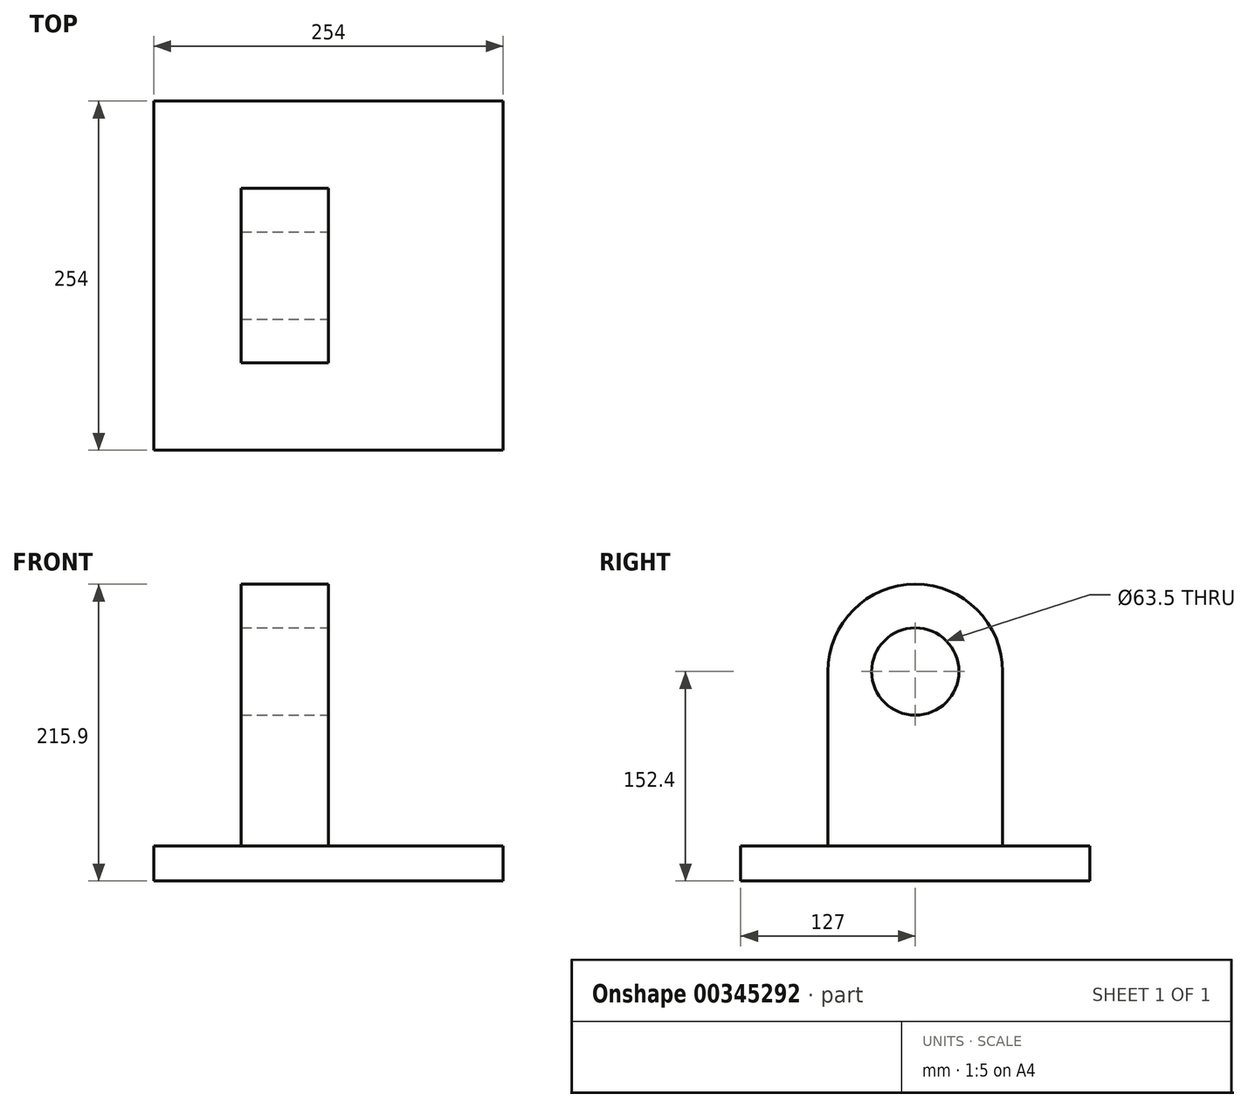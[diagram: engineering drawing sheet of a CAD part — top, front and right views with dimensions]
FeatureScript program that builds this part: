
annotation { "Feature Type Name" : "Feature", "Feature Type Description" : "" }
export const myFeature = defineFeature(function(context is Context, id is Id, definition is map)
    precondition{}
    {
        {
            var Q0;
            Q0=qCreatedBy(makeId("Top.planeOp"),FACE);
            var sketch = newSketch(context, id + "F0", { "sketchPlane" : qUnion([Q0])});
            skLineSegment(sketch, "E0.bottom", {"start": v(127, -127) * mm, "end": v(-127, -127) * mm});
            skLineSegment(sketch, "E0.top", {"start": v(127, 127) * mm, "end": v(-127, 127) * mm});
            skLineSegment(sketch, "E0.left", {"start": v(127, -127) * mm, "end": v(127, 127) * mm});
            skLineSegment(sketch, "E0.right", {"start": v(-127, -127) * mm, "end": v(-127, 127) * mm});
            skPoint(sketch, "E0.middle", {"position": v(0, 0) * mm});
            skSolve(sketch);
        }
        {
            var Q0;
            Q0=makeQuery(id+"F0.imprint","IMPRINT",FACE,{"disambiguationData":[TD([[makeQuery(id+"F0.imprint","IMPRINT",EDGE,{"derivedFrom":sQuery(id+"F0.wireOp",EDGE,"E0.bottom")}),-1.0]])]});
            extrude(context, id + "F1", {"entities" : qUnion([Q0]), "depth" : 25.4 * mm});
        }
        {
            var Q0;
            Q0=makeQuery(id+"F1.opExtrude","CAP_FACE",FACE,{"disambiguationData":[OSD([sQuery(id+"F0.wireOp",EDGE,"E0.bottom"),sQuery(id+"F0.wireOp",EDGE,"E0.top"),sQuery(id+"F0.wireOp",EDGE,"E0.left"),sQuery(id+"F0.wireOp",EDGE,"E0.right")])],"isStart":false});
            var sketch = newSketch(context, id + "F2", { "sketchPlane" : qUnion([Q0])});
            skLineSegment(sketch, "E1.bottom", {"start": v(0, -63.5) * mm, "end": v(-63.5, -63.5) * mm});
            skLineSegment(sketch, "E1.top", {"start": v(0, 63.5) * mm, "end": v(-63.5, 63.5) * mm});
            skLineSegment(sketch, "E1.right", {"start": v(-63.5, -63.5) * mm, "end": v(-63.5, 63.5) * mm});
            skPoint(sketch, "E1.middle", {"position": v(0, 0) * mm});
            skLineSegment(sketch, "E2", {"start": v(0, 63.5) * mm, "end": v(0, -63.5) * mm});
            skSolve(sketch);
        }
        {
            var Q0;
            Q0 = qSketchRegion(id + "F2", true);
            var Q1;
            Q1=makeQuery(id+"F1.opExtrude","CAP_FACE",FACE,{"disambiguationData":[OSD([sQuery(id+"F0.wireOp",EDGE,"E0.bottom"),sQuery(id+"F0.wireOp",EDGE,"E0.top"),sQuery(id+"F0.wireOp",EDGE,"E0.left"),sQuery(id+"F0.wireOp",EDGE,"E0.right")])],"isStart":false});
            extrude(context, id + "F3", {"entities" : qUnion([Q0]), "operationType" : NewBodyOperationType.ADD, "depth" : 127 * mm});
        }
        {
            var Q0;
            Q0=makeQuery(id+"F3.opExtrude","SWEPT_FACE",FACE,{"disambiguationData":[OSD([sQuery(id+"F2.wireOp",EDGE,"E1.right")])]});
            var sketch = newSketch(context, id + "F4", { "sketchPlane" : qUnion([Q0])});
            skCircle(sketch, "E3", {"center": v(0, 152.4) * mm, "radius": 63.5 * mm});
            skSolve(sketch);
        }
        {
            var Q0;
            Q0 = qSketchRegion(id + "F4", true);
            extrude(context, id + "F5", {"entities" : qUnion([Q0]), "operationType" : NewBodyOperationType.ADD, "oppositeDirection" : true, "depth" : 63.5 * mm});
        }
        {
            var Q0;
            Q0=makeQuery(id+"F5.boolean.opBoolean","MERGE",FACE,{"derivedFrom":[makeQuery(id+"F3.opExtrude","SWEPT_FACE",FACE,{"disambiguationData":[OSD([sQuery(id+"F2.wireOp",EDGE,"E2")])]}),makeQuery(id+"F5.opExtrude","CAP_FACE",FACE,{"disambiguationData":[OSD([sQuery(id+"F4.wireOp",EDGE,"E3")])],"isStart":false})]});
            var sketch = newSketch(context, id + "F6", { "sketchPlane" : qUnion([Q0])});
            skCircle(sketch, "E4", {"center": v(0, 152.4) * mm, "radius": 31.75 * mm});
            skSolve(sketch);
        }
        {
            var Q0;
            Q0 = qSketchRegion(id + "F6", true);
            var Q1;
            Q1=makeQuery(id+"F5.boolean.opBoolean","MERGE",FACE,{"derivedFrom":[makeQuery(id+"F3.opExtrude","SWEPT_FACE",FACE,{"disambiguationData":[OSD([sQuery(id+"F2.wireOp",EDGE,"E1.right")])]}),makeQuery(id+"F5.opExtrude","CAP_FACE",FACE,{"disambiguationData":[OSD([sQuery(id+"F4.wireOp",EDGE,"E3")])],"isStart":true})]});
            extrude(context, id + "F7", {"entities" : qUnion([Q0]), "operationType" : NewBodyOperationType.REMOVE, "endBound" : BoundingType.UP_TO_SURFACE, "oppositeDirection" : true, "endBoundEntityFace" : qUnion([Q1]), "depth" : 25.4 * mm});
        }
    });
